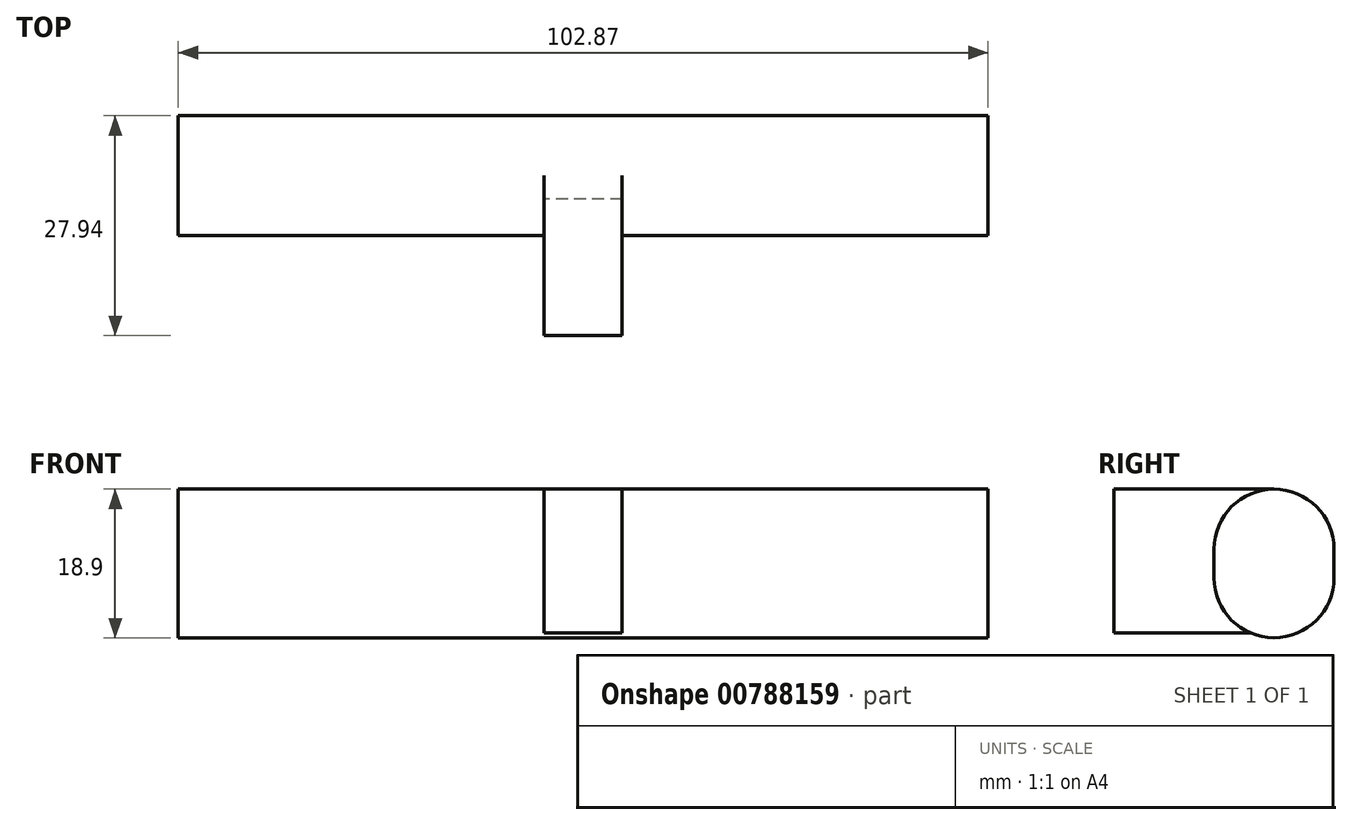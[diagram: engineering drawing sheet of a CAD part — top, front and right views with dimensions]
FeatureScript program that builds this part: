
annotation { "Feature Type Name" : "Feature", "Feature Type Description" : "" }
export const myFeature = defineFeature(function(context is Context, id is Id, definition is map)
    precondition{}
    {
        {
            var Q0;
            Q0=qCreatedBy(makeId("Front.planeOp"),FACE);
            var sketch = newSketch(context, id + "F0", { "sketchPlane" : qUnion([Q0])});
            skLineSegment(sketch, "E0.bottom", {"start": v(0, 0) * mm, "end": v(-9.9, 0) * mm});
            skLineSegment(sketch, "E0.top", {"start": v(0, 18.29) * mm, "end": v(-9.9, 18.29) * mm});
            skLineSegment(sketch, "E0.left", {"start": v(0, 0) * mm, "end": v(0, 18.29) * mm});
            skLineSegment(sketch, "E0.right", {"start": v(-9.9, 0) * mm, "end": v(-9.9, 18.29) * mm});
            skSolve(sketch);
        }
        {
            var Q0;
            Q0=makeQuery(id+"F0.imprint","IMPRINT",FACE,{"disambiguationData":[TD([[makeQuery(id+"F0.imprint","IMPRINT",EDGE,{"derivedFrom":sQuery(id+"F0.wireOp",EDGE,"E0.bottom")}),-1.0]])]});
            extrude(context, id + "F1", {"entities" : qUnion([Q0]), "endBound" : BoundingType.SYMMETRIC, "depth" : 12.7 * mm, "offsetDistance" : 25.4 * mm});
        }
        {
            var Q0;
            Q0=makeQuery(id+"F1.opExtrude","CAP_FACE",FACE,{"disambiguationData":[OSD([sQuery(id+"F0.wireOp",EDGE,"E0.bottom"),sQuery(id+"F0.wireOp",EDGE,"E0.top"),sQuery(id+"F0.wireOp",EDGE,"E0.left"),sQuery(id+"F0.wireOp",EDGE,"E0.right")])],"isStart":true});
            var sketch = newSketch(context, id + "F2", { "sketchPlane" : qUnion([Q0])});
            skLineSegment(sketch, "E1.bottom", {"start": v(-46.48, 18.29) * mm, "end": v(56.39, 18.29) * mm});
            skLineSegment(sketch, "E1.top", {"start": v(-46.48, -0.6) * mm, "end": v(56.39, -0.6) * mm});
            skLineSegment(sketch, "E1.left", {"start": v(-46.48, 18.29) * mm, "end": v(-46.48, -0.6) * mm});
            skLineSegment(sketch, "E1.right", {"start": v(56.39, 18.29) * mm, "end": v(56.39, -0.6) * mm});
            skPoint(sketch, "E1.middle", {"position": v(4.95, 8.84) * mm});
            skPoint(sketch, "E1.middle.positionSnap0", {"position": v(4.95, 18.29) * mm});
            skPoint(sketch, "E1.cornerSnap0", {"position": v(4.95, 18.29) * mm});
            skPoint(sketch, "E1.centerSnap0", {"position": v(4.95, 18.29) * mm});
            skSolve(sketch);
        }
        {
            var Q0;
            Q0=makeQuery(id+"F2.imprint","IMPRINT",FACE,{"disambiguationData":[TD([[makeQuery(id+"F2.imprint","IMPRINT",EDGE,{"derivedFrom":sQuery(id+"F2.wireOp",EDGE,"E1.top")}),1.0]])]});
            var Q1;
            Q1=makeQuery(id+"F2.imprint","IMPRINT",FACE,{"disambiguationData":[TD([[makeQuery(id+"F2.imprint","IMPRINT",EDGE,{"derivedFrom":makeQuery(id+"F1.opExtrude","CAP_EDGE",EDGE,{"disambiguationData":[OSD([sQuery(id+"F0.wireOp",EDGE,"E0.bottom")])],"isStart":true})}),1.0]])]});
            extrude(context, id + "F3", {"entities" : qUnion([Q0, Q1]), "operationType" : NewBodyOperationType.ADD, "depth" : 15.24 * mm, "offsetDistance" : 25.4 * mm});
        }
        {
            var Q0;
            Q0=makeQuery(id+"F3.opExtrude","CAP_EDGE",EDGE,{"disambiguationData":[OSD([sQuery(id+"F2.wireOp",EDGE,"E1.top")])],"isStart":true});
            var Q1;
            Q1=makeQuery(id+"F3.opExtrude","CAP_EDGE",EDGE,{"disambiguationData":[OSD([sQuery(id+"F2.wireOp",EDGE,"E1.top")])],"isStart":false});
            var Q2;
            {var subQ1=sQuery(id+"F2.wireOp",EDGE,"E1.bottom");Q2=makeQuery(id+"F3.boolean.opBoolean","SPLIT",EDGE,{"disambiguationData":[TD([makeQuery(id+"F1.opExtrude","SWEPT_FACE",FACE,{"disambiguationData":[OSD([sQuery(id+"F0.wireOp",EDGE,"E0.right")])]})])],"derivedFrom":makeQuery(id+"F3.opExtrude","CAP_EDGE",EDGE,{"disambiguationData":[OSD([subQ1])],"isStart":true})});}
            var Q3;
            Q3=makeQuery(id+"F3.opExtrude","CAP_EDGE",EDGE,{"disambiguationData":[OSD([sQuery(id+"F2.wireOp",EDGE,"E1.bottom")])],"isStart":false});
            var Q4;
            {var subQ1=sQuery(id+"F2.wireOp",EDGE,"E1.bottom");Q4=makeQuery(id+"F3.boolean.opBoolean","SPLIT",EDGE,{"disambiguationData":[TD([makeQuery(id+"F1.opExtrude","SWEPT_FACE",FACE,{"disambiguationData":[OSD([sQuery(id+"F0.wireOp",EDGE,"E0.left")])]})])],"derivedFrom":makeQuery(id+"F3.opExtrude","CAP_EDGE",EDGE,{"disambiguationData":[OSD([subQ1])],"isStart":true})});}
            fillet(context, id + "F4", {"entities" : qUnion([Q0, Q1, Q2, Q3, Q4]), "radius" : 7.62 * mm, "tangentPropagation" : true, "allowEdgeOverflow" : false});
        }
    });
